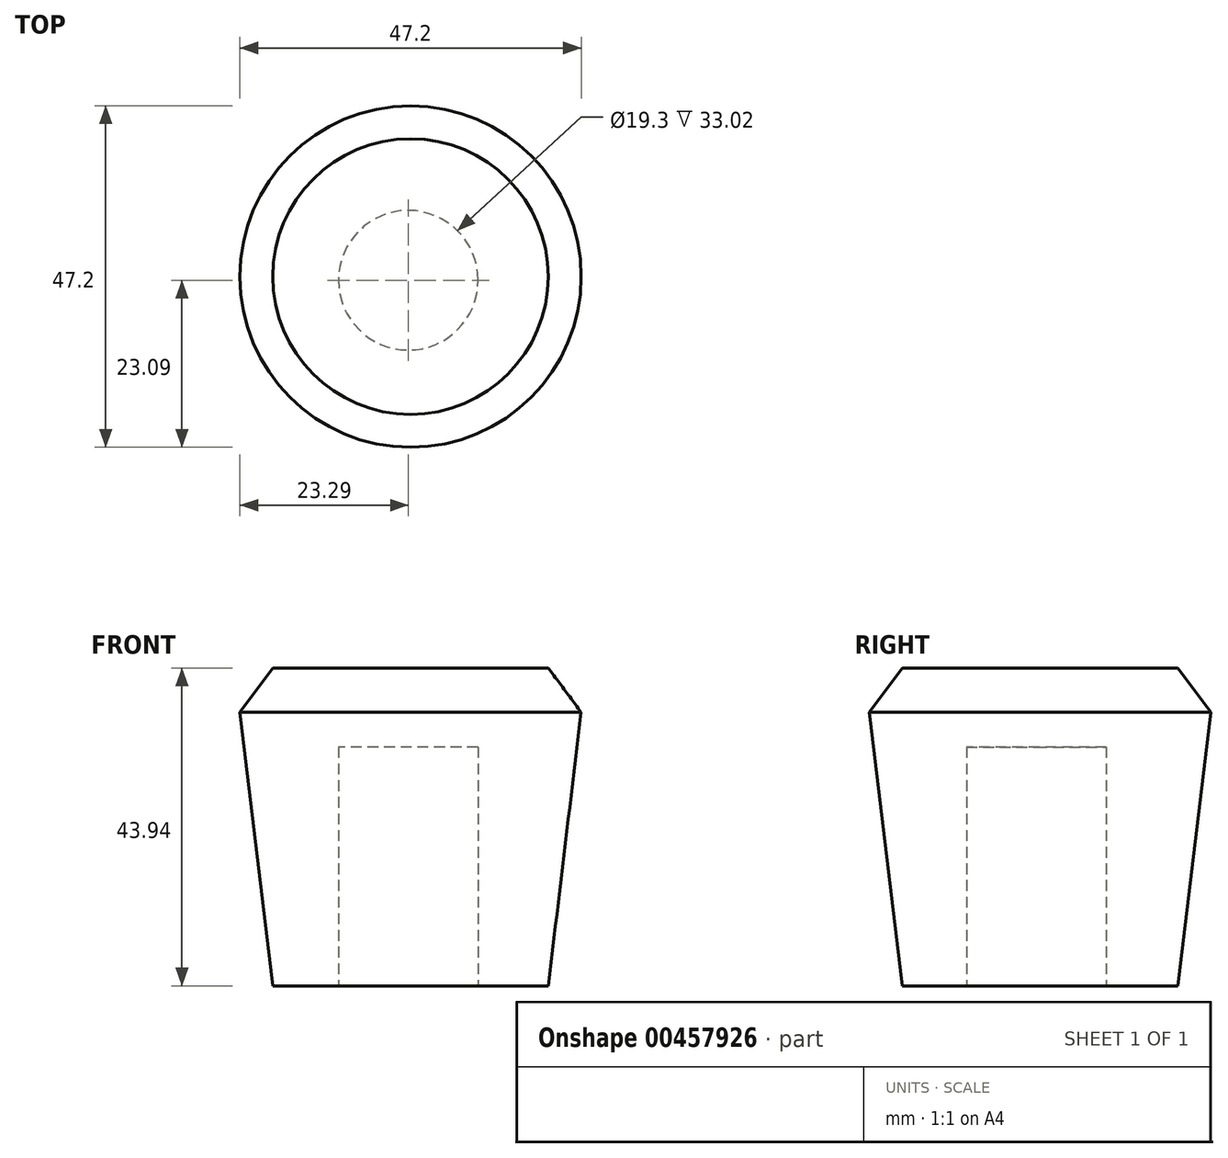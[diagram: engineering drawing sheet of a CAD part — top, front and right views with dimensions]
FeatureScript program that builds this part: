
annotation { "Feature Type Name" : "Feature", "Feature Type Description" : "" }
export const myFeature = defineFeature(function(context is Context, id is Id, definition is map)
    precondition{}
    {
        {
            var Q0;
            Q0=qCreatedBy(makeId("Front.planeOp"),FACE);
            var sketch = newSketch(context, id + "F0", { "sketchPlane" : qUnion([Q0])});
            skLineSegment(sketch, "E0", {"start": v(-50, 0) * mm, "end": v(-69.05, 0) * mm});
            skLineSegment(sketch, "E1", {"start": v(-69.05, 0) * mm, "end": v(-73.6, 37.83) * mm});
            skLineSegment(sketch, "E2", {"start": v(-73.6, 37.83) * mm, "end": v(-69.05, 43.94) * mm});
            skLineSegment(sketch, "E3", {"start": v(-69.05, 43.94) * mm, "end": v(-50, 43.94) * mm});
            skLineSegment(sketch, "E4", {"start": v(-50, 43.94) * mm, "end": v(-50, 0) * mm});
            skSolve(sketch);
        }
        {
            var Q0;
            Q0 = qSketchRegion(id + "F0", true);
            var Q1;
            Q1=sQuery(id+"F0.wireOp",EDGE,"E4");
            revolve(context, id + "F1", {"entities" : qUnion([Q0]), "axis" : qUnion([Q1]), "revolveType" : RevolveType.FULL});
        }
        {
            var Q0;
            Q0=qCreatedBy(makeId("Top.planeOp"),FACE);
            var sketch = newSketch(context, id + "F2", { "sketchPlane" : qUnion([Q0])});
            skCircle(sketch, "E5", {"center": v(-50.31, -0.51) * mm, "radius": 9.65 * mm});
            skSolve(sketch);
        }
        {
            var Q0;
            Q0=makeQuery(id+"F2.imprint","IMPRINT",FACE,{"disambiguationData":[TD([[makeQuery(id+"F2.imprint","IMPRINT",EDGE,{"derivedFrom":sQuery(id+"F2.wireOp",EDGE,"E5")}),1.0]])]});
            extrude(context, id + "F3", {"entities" : qUnion([Q0]), "operationType" : NewBodyOperationType.REMOVE, "depth" : 33.02 * mm});
        }
    });
